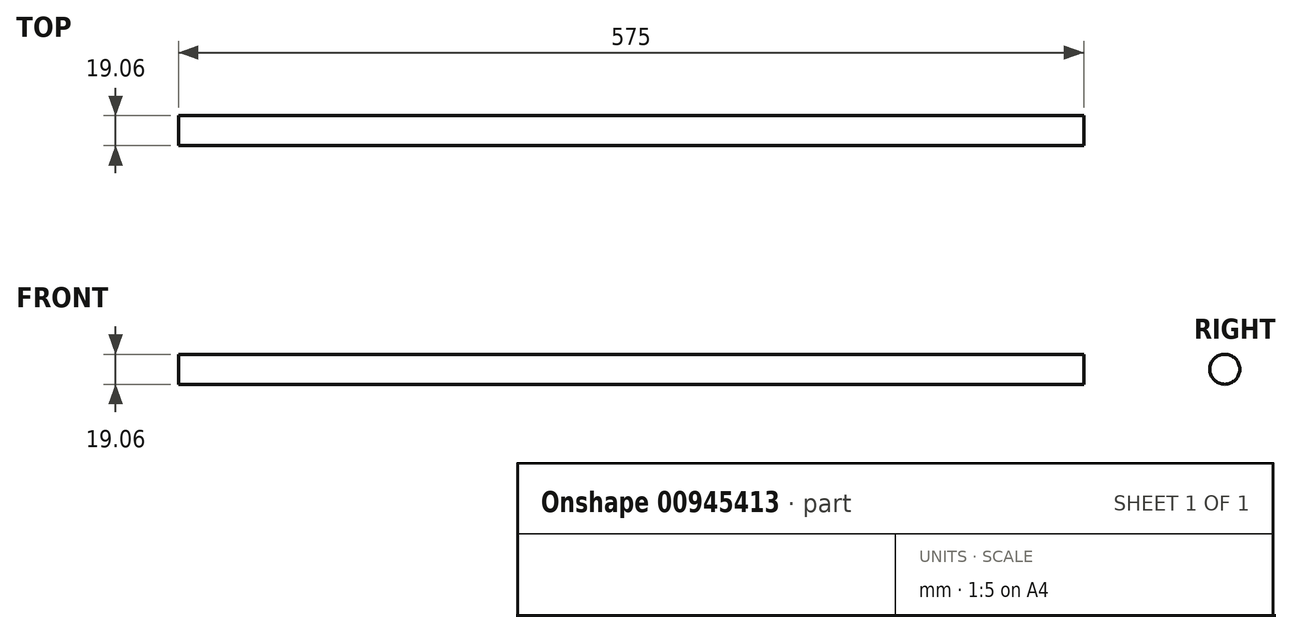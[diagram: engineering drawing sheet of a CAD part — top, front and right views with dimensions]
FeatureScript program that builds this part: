
annotation { "Feature Type Name" : "Feature", "Feature Type Description" : "" }
export const myFeature = defineFeature(function(context is Context, id is Id, definition is map)
    precondition{}
    {
        {
            var Q0;
            Q0=qCreatedBy(makeId("Right.planeOp"),FACE);
            var sketch = newSketch(context, id + "F0", { "sketchPlane" : qUnion([Q0])});
            skCircle(sketch, "E0", {"center": v(0, 0) * mm, "radius": 9.53 * mm});
            skSolve(sketch);
        }
        {
            var Q0;
            Q0=sQuery(id+"F0.wireOp",EDGE,"E0");
            extrude(context, id + "F1", {"bodyType" : ToolBodyType.SURFACE, "surfaceEntities" : qUnion([Q0]), "depth" : 575 * mm, "offsetDistance" : 25.4 * mm});
        }
    });
